# Revit family: CADS_Vent-Axia_Lo-CarbonSentinel_Econiq_S_MVHR
name_source: partatom
category: Mechanical Equipment
units: mm (PartAtom-declared; Revit-internal decimal feet)

## family parameters
Always vertical = Yes
Cut with Voids When Loaded = No
OmniClass Number = 23.75.00.00
OmniClass Title = Climate Control (HVAC)
Part Type = Normal
Room Calculation Point = No
Round Connector Dimension = Use Diameter
Shared = No
Work Plane-Based = No

## types (2) — shared parameters
AirflowRateRange = 115.0 L/s
AssemblyPlace = FACTORY
AssetType = Fixed
Category = Pr_60_60_36:Heat recovery distribution equipment
Color = White
Description = Sentinel Econiq S
DevelopedFor = Vent-Axia
DurationUnit = year
ExpectedLife = 20
ExpectedServiceLife = 15
Fitting Type = Ignore
GrossWeight = 27.00 kg
HasProtectiveEarth = Yes
IP_Code = IPX2
IfcExportAs = IfcAirToAirHeatRecoveryType
IfcExportType = USERDEFINED
IsExtendedWarranty = No
Manufacturer = Vent-Axia Limited
Material = ABS Plastic
Model = 499883
ModelNumber = 499883
ModelReference = Sentinel Econiq S
Name = MVHR Unit
NominalHeight = 760 mm  [stored 2.49344 ft]
NominalLength = 660 mm  [stored 2.16535 ft]
NominalWidth = 443 mm  [stored 1.45341 ft]
NumberOfPoles = 1
ProductionYear = 2020
Quantity = 1
RatedVoltage = 240 V
ServiceLifeDuration = 20
Shape = Rectangular
Size = 443mm x 660mm x 760mm 
285mm x 550mm x 550mm
SpigotDiameter = 125 mm  [stored 0.410105 ft]
SpigotHeight = 63 mm  [stored 0.206693 ft]
Status = New
TemperatureRange = -20°C to+40°C
Type Image = CADS_Vent-Axia_Lo-CarbonSentinel_Small_MVHR.jpg
Version = 1.0
WarrantyDurationLabor = 2
WarrantyDurationMotors = 5
WarrantyDurationParts = 2
WarrantyDurationUnit = year
WorkingPressure = 0.0 Pa
zero-valued in all types: CADS_Index, Default Elevation

## per-type parameters (varying)
| type | Apparent Load | LeftHand | RatedCurrent |
| Sentinel Econiq S Right Hand | 690 VA | No | 3 A |
| Sentinel Econiq S Left Hand | 0 VA | Yes | 0 A |

note: [stored X ft] marks values corroborated as IEEE doubles in the binary element streams (Revit-internal decimal feet)

## geometry (parser evidence)
native form markers: Sweep x4
no freeform markers — native parametric forms only
